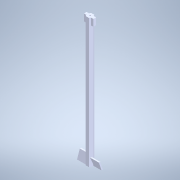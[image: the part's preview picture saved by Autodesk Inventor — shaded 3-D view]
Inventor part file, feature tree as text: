
AUTODESK INVENTOR PART (.ipt)
format: ipt  version: 2022 (Build 260153000, 153)  size: 132,608 bytes
history: native  units: mm
features: extrude x1, sketch x1, other x1
ambient origin geometry x8: Origin, YZ Plane, XZ Plane, XY Plane, X Axis, Y Axis, Z Axis, Center Point
bodies: Solid1 (feature_tree)
feature tree (3):
  extrude  "Extrusion1"  Depth=1.0mm TaperAngle=0.0deg
  sketch  "Sketch1"  dims[d0=1.0mm d1=1.0mm d2=0.0mm]
  other  "Boss-Extrude4"
